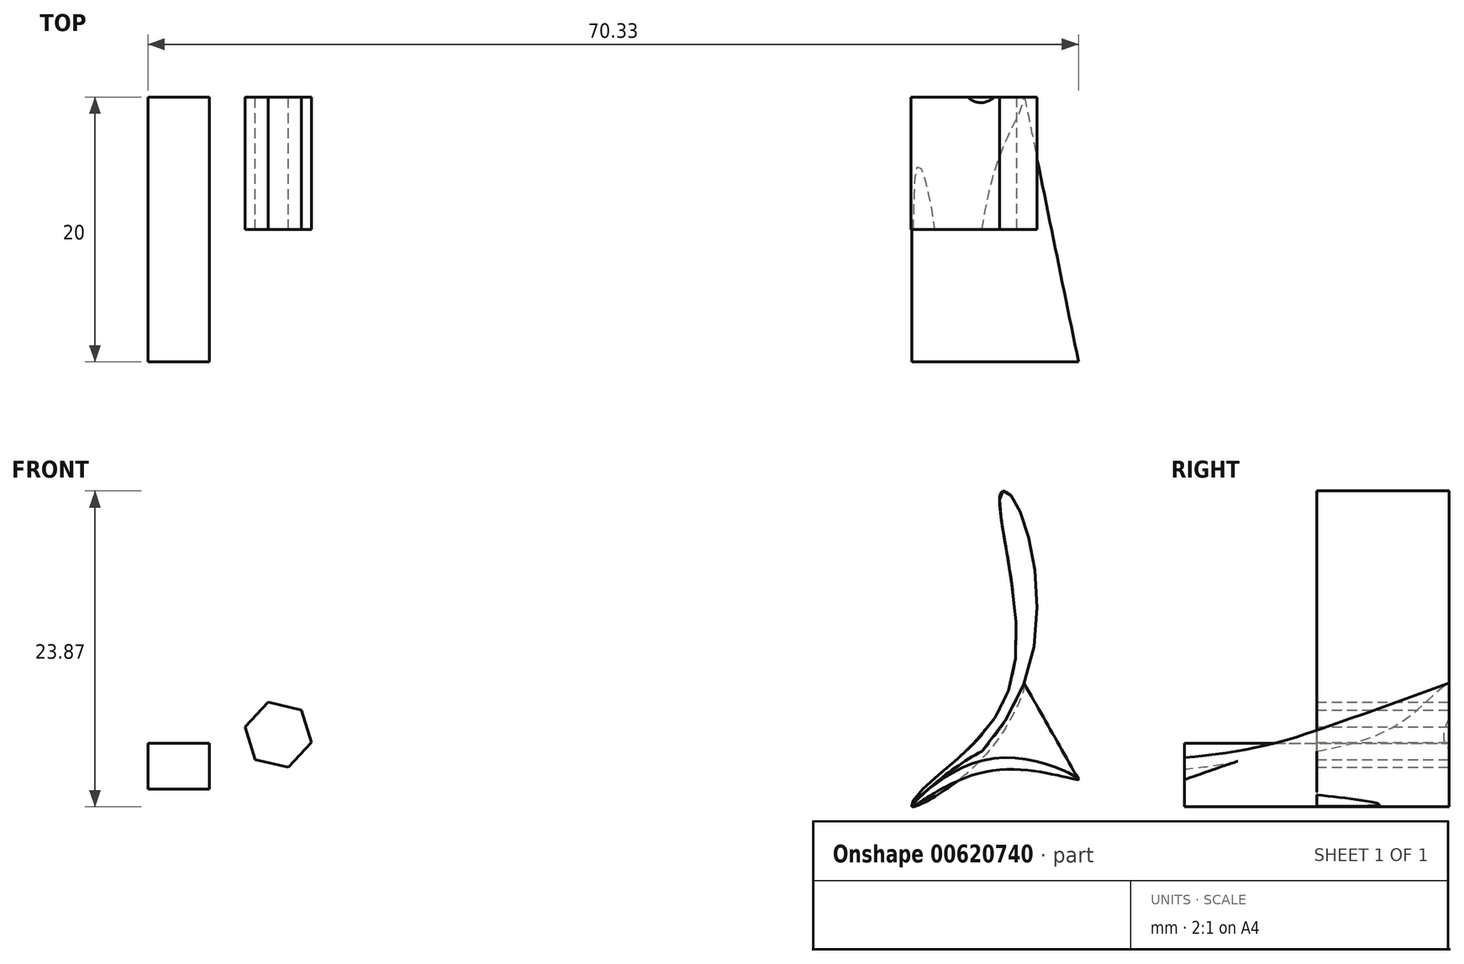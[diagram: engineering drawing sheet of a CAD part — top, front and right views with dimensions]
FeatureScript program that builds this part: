
annotation { "Feature Type Name" : "Feature", "Feature Type Description" : "" }
export const myFeature = defineFeature(function(context is Context, id is Id, definition is map)
    precondition{}
    {
        {
            var Q0;
            Q0=qCreatedBy(makeId("Front.planeOp"),FACE);
            var sketch = newSketch(context, id + "F0", { "sketchPlane" : qUnion([Q0])});
            skCircle(sketch, "E0.cCircle", {"center": v(-47.89, 5.42) * mm, "radius": 2.22 * mm, "construction": true});
            skLineSegment(sketch, "E0.0", {"start": v(-45.38, 4.84) * mm, "end": v(-47.14, 2.96) * mm});
            skLineSegment(sketch, "E0.1", {"start": v(-47.14, 2.96) * mm, "end": v(-49.64, 3.54) * mm});
            skLineSegment(sketch, "E0.2", {"start": v(-49.64, 3.54) * mm, "end": v(-50.39, 6) * mm});
            skLineSegment(sketch, "E0.3", {"start": v(-50.39, 6) * mm, "end": v(-48.63, 7.87) * mm});
            skLineSegment(sketch, "E0.4", {"start": v(-48.63, 7.87) * mm, "end": v(-46.13, 7.3) * mm});
            skLineSegment(sketch, "E0.5", {"start": v(-46.13, 7.3) * mm, "end": v(-45.38, 4.84) * mm});
            skPoint(sketch, "E0.0.midPoint", {"position": v(-46.26, 3.9) * mm});
            skSolve(sketch);
        }
        {
            var Q0;
            Q0 = qSketchRegion(id + "F0", true);
            extrude(context, id + "F1", {"entities" : qUnion([Q0]), "depth" : 10 * mm, "offsetDistance" : 25 * mm});
        }
        {
            var Q0;
            Q0=qCreatedBy(makeId("Front.planeOp"),FACE);
            var sketch = newSketch(context, id + "F2", { "sketchPlane" : qUnion([Q0])});
            skLineSegment(sketch, "E1.bottom", {"start": v(-57.74, 4.77) * mm, "end": v(-53.09, 4.77) * mm});
            skLineSegment(sketch, "E1.top", {"start": v(-57.74, 1.3) * mm, "end": v(-53.09, 1.3) * mm});
            skLineSegment(sketch, "E1.left", {"start": v(-57.74, 4.77) * mm, "end": v(-57.74, 1.3) * mm});
            skLineSegment(sketch, "E1.right", {"start": v(-53.09, 4.77) * mm, "end": v(-53.09, 1.3) * mm});
            skSolve(sketch);
        }
        {
            var Q0;
            Q0=makeQuery(id+"F2.imprint","IMPRINT",FACE,{"disambiguationData":[TD([[makeQuery(id+"F2.imprint","IMPRINT",EDGE,{"derivedFrom":sQuery(id+"F2.wireOp",EDGE,"E1.bottom")}),-1.0]])]});
            extrude(context, id + "F3", {"entities" : qUnion([Q0]), "depth" : 20 * mm, "offsetDistance" : 25 * mm});
        }
        {
            var Q0;
            Q0=qCreatedBy(makeId("Front.planeOp"),FACE);
            var sketch = newSketch(context, id + "F4", { "sketchPlane" : qUnion([Q0])});
            skFitSpline(sketch, "E2", {"points": [v(0, 0) * mm, v(8.43, 9.16) * mm, v(7.39, 23.63) * mm, v(6.7, 23.63) * mm, v(7.62, 9.85) * mm, v(1.02, 1.52) * mm, v(0, 0) * mm]});
            skSolve(sketch);
        }
        {
            var Q0;
            Q0 = qSketchRegion(id + "F4", true);
            extrude(context, id + "F5", {"entities" : qUnion([Q0]), "depth" : 10 * mm, "offsetDistance" : 25 * mm});
        }
        {
            var Q0;
            Q0=qCreatedBy(makeId("Front.planeOp"),FACE);
            var sketch = newSketch(context, id + "F6", { "sketchPlane" : qUnion([Q0])});
            skFitSpline(sketch, "E3", {"points": [v(0, 0) * mm, v(4.66, 4.78) * mm, v(8.48, 9.3) * mm, v(5.47, 3.8) * mm, v(0, 0) * mm]});
            skSolve(sketch);
        }
        {
            var Q0;
            Q0=makeQuery(id+"F3.opExtrude","CAP_FACE",FACE,{"disambiguationData":[OSD([sQuery(id+"F2.wireOp",EDGE,"E1.bottom"),sQuery(id+"F2.wireOp",EDGE,"E1.top"),sQuery(id+"F2.wireOp",EDGE,"E1.left"),sQuery(id+"F2.wireOp",EDGE,"E1.right")])],"isStart":false});
            var sketch = newSketch(context, id + "F7", { "sketchPlane" : qUnion([Q0])});
            skFitSpline(sketch, "E4", {"points": [v(0, 0) * mm, v(5.93, 3.6) * mm, v(12.6, 2.04) * mm, v(5.88, 2.68) * mm, v(0, 0) * mm]});
            skSolve(sketch);
        }
        {
            var Q1;
            Q1 = qSketchRegion(id + "F6", true);
            var Q2;
            Q2 = qSketchRegion(id + "F7", true);
            loft(context, id + "F8", {"operationType" : NewBodyOperationType.ADD, "sheetProfilesArray" : [{ "sheetProfileEntities" : qUnion([Q1]) }, { "sheetProfileEntities" : qUnion([Q2]) }]});
        }
    });
